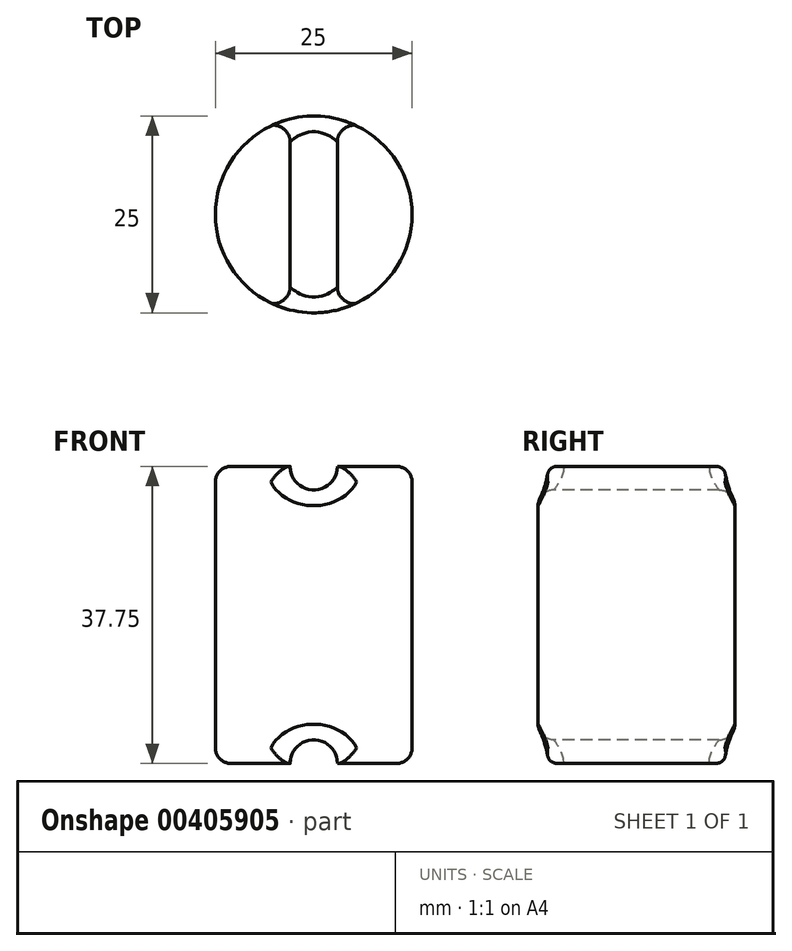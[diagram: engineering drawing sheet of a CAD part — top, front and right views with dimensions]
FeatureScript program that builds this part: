
annotation { "Feature Type Name" : "Feature", "Feature Type Description" : "" }
export const myFeature = defineFeature(function(context is Context, id is Id, definition is map)
    precondition{}
    {
        {
            var Q0;
            Q0=qCreatedBy(makeId("Top.planeOp"),FACE);
            var sketch = newSketch(context, id + "F0", { "sketchPlane" : qUnion([Q0])});
            skCircle(sketch, "E0", {"center": v(0, 0) * mm, "radius": 12.5 * mm});
            skSolve(sketch);
        }
        {
            var Q0;
            Q0 = qSketchRegion(id + "F0", true);
            extrude(context, id + "F1", {"entities" : qUnion([Q0]), "depth" : 37.75 * mm});
        }
        {
            var Q0;
            Q0=qCreatedBy(makeId("Front.planeOp"),FACE);
            var sketch = newSketch(context, id + "F2", { "sketchPlane" : qUnion([Q0])});
            skLineSegment(sketch, "E1.0", {"start": v(-12.5, 37.75) * mm, "end": v(12.5, 37.75) * mm, "construction": true});
            skLineSegment(sketch, "E2", {"start": v(-12.5, 0) * mm, "end": v(-12.5, 37.75) * mm, "construction": true});
            skLineSegment(sketch, "E3", {"start": v(12.5, 37.75) * mm, "end": v(12.5, 0) * mm, "construction": true});
            skLineSegment(sketch, "E4.0", {"start": v(-12.5, 0) * mm, "end": v(12.5, 0) * mm, "construction": true});
            skCircle(sketch, "E5", {"center": v(0, 37.75) * mm, "radius": 3 * mm});
            skCircle(sketch, "E6", {"center": v(0, 0) * mm, "radius": 3 * mm});
            skSolve(sketch);
        }
        {
            var Q0;
            Q0 = qSketchRegion(id + "F2", true);
            extrude(context, id + "F3", {"entities" : qUnion([Q0]), "operationType" : NewBodyOperationType.REMOVE, "endBound" : BoundingType.SYMMETRIC, "oppositeDirection" : true, "depth" : 30 * mm});
        }
        {
            var Q0;
            Q0=makeQuery(id+"F3.boolean.opBoolean","SPLIT",EDGE,{"disambiguationData":[OD(0.0)],"derivedFrom":makeQuery(id+"F1.opExtrude","CAP_EDGE",EDGE,{"disambiguationData":[OSD([sQuery(id+"F0.wireOp",EDGE,"E0")])],"isStart":false})});
            var Q1;
            Q1=makeQuery(id+"F3.boolean.opBoolean","SPLIT",EDGE,{"disambiguationData":[OD(0.0)],"derivedFrom":makeQuery(id+"F1.opExtrude","CAP_EDGE",EDGE,{"disambiguationData":[OSD([sQuery(id+"F0.wireOp",EDGE,"E0")])],"isStart":true})});
            var Q2;
            Q2=makeQuery(id+"F3.boolean.opBoolean","SPLIT",EDGE,{"disambiguationData":[OD(1.0)],"derivedFrom":makeQuery(id+"F1.opExtrude","CAP_EDGE",EDGE,{"disambiguationData":[OSD([sQuery(id+"F0.wireOp",EDGE,"E0")])],"isStart":true})});
            var Q3;
            Q3=makeQuery(id+"F3.boolean.opBoolean","SPLIT",EDGE,{"disambiguationData":[OD(1.0)],"derivedFrom":makeQuery(id+"F1.opExtrude","CAP_EDGE",EDGE,{"disambiguationData":[OSD([sQuery(id+"F0.wireOp",EDGE,"E0")])],"isStart":false})});
            var Q4;
            Q4=makeQuery(id+"F3.boolean.opBoolean","INTERSECT",EDGE,{"disambiguationData":[OD(0.0)],"derivedFrom":[makeQuery(id+"F1.opExtrude","SWEPT_FACE",FACE,{"disambiguationData":[OSD([sQuery(id+"F0.wireOp",EDGE,"E0")])]}),makeQuery(id+"F3.opExtrude","SWEPT_FACE",FACE,{"disambiguationData":[OSD([sQuery(id+"F2.wireOp",EDGE,"E5")])]})]});
            var Q5;
            Q5=makeQuery(id+"F3.boolean.opBoolean","INTERSECT",EDGE,{"disambiguationData":[OD(1.0)],"derivedFrom":[makeQuery(id+"F1.opExtrude","SWEPT_FACE",FACE,{"disambiguationData":[OSD([sQuery(id+"F0.wireOp",EDGE,"E0")])]}),makeQuery(id+"F3.opExtrude","SWEPT_FACE",FACE,{"disambiguationData":[OSD([sQuery(id+"F2.wireOp",EDGE,"E5")])]})]});
            var Q6;
            Q6=makeQuery(id+"F3.boolean.opBoolean","INTERSECT",EDGE,{"disambiguationData":[OD(1.0)],"derivedFrom":[makeQuery(id+"F1.opExtrude","SWEPT_FACE",FACE,{"disambiguationData":[OSD([sQuery(id+"F0.wireOp",EDGE,"E0")])]}),makeQuery(id+"F3.opExtrude","SWEPT_FACE",FACE,{"disambiguationData":[OSD([sQuery(id+"F2.wireOp",EDGE,"E6")])]})]});
            var Q7;
            Q7=makeQuery(id+"F3.boolean.opBoolean","INTERSECT",EDGE,{"disambiguationData":[OD(0.0)],"derivedFrom":[makeQuery(id+"F1.opExtrude","SWEPT_FACE",FACE,{"disambiguationData":[OSD([sQuery(id+"F0.wireOp",EDGE,"E0")])]}),makeQuery(id+"F3.opExtrude","SWEPT_FACE",FACE,{"disambiguationData":[OSD([sQuery(id+"F2.wireOp",EDGE,"E6")])]})]});
            fillet(context, id + "F4", {"entities" : qUnion([Q0, Q1, Q2, Q3, Q4, Q5, Q6, Q7]), "radius" : 2 * mm, "tangentPropagation" : true, "allowEdgeOverflow" : false});
        }
    });
